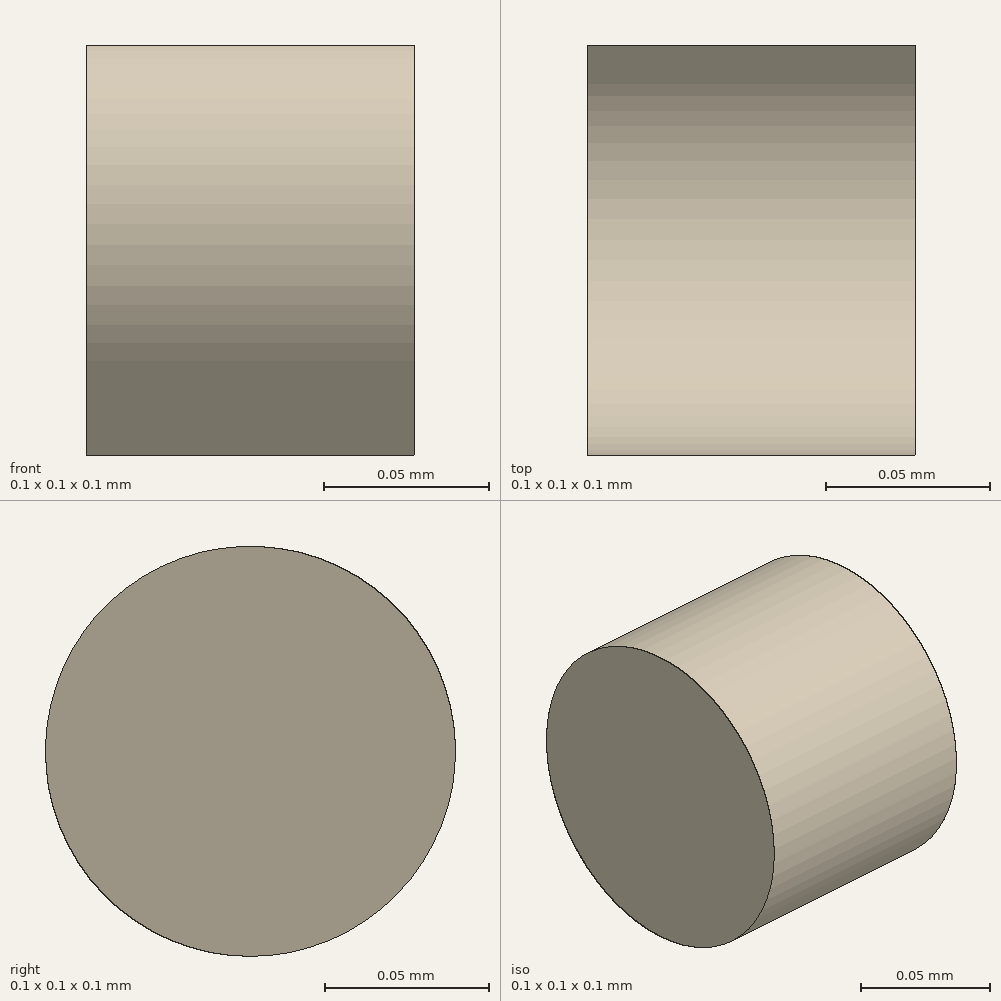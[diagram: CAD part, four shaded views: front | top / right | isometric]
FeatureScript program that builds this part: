
annotation { "Feature Type Name" : "Feature", "Feature Type Description" : "" }
export const myFeature = defineFeature(function(context is Context, id is Id, definition is map)
    precondition{}
    {
        {
            var Q0;
            Q0=qCreatedBy(makeId("Right.planeOp"),FACE);
            var sketch = newSketch(context, id + "F0", { "sketchPlane" : qUnion([Q0])});
            skCircle(sketch, "E0", {"center": v(0, 0) * mm, "radius": 0.06 * mm});
            skSolve(sketch);
        }
        {
            var Q0;
            Q0=qSketchRegion(id+"F0",true);
            extrude(context, id + "F1", {"entities" : qUnion([Q0]), "flatOperationType" : FlatOperationType.REMOVE, "depth" : 0.1 * mm, "offsetDistance" : 25 * mm, "domain" : OperationDomain.MODEL});
        }
    });
